# Revit family: MR-1002
name_source: partatom
category: Plumbing Fixtures
revit_build: Autodesk Revit 2014 (Build: 20130308_1515(x64)
units: mm (PartAtom-declared; Revit-internal decimal feet)

## types (1)
- MR-1002
    Brass Chromed = Brass
    CW Connection = Yes
    Data Sheet = http://helvex.com
    Description = Vértika Tub And/Or Shower Two Handle In-Wall Faucet
    Features = Threaded Body, Val-Vex Level Left And Right To ¼" Turn To Ceramic Disc; Includes Setting Tool For Maintenance
    HW Connection = Yes
    Inlet Threads = ½" - 14 NPT
    Installation Adjustment = 0.315" (8 mm) Max.
    Instructive = http://helvex.com
    Manufacturer = HELVEX
    Max. Working Pressure = 85.3 psi
    Min. Working Pressure = 2.9 psi
    Model = MR-1002
    Satin = Satín
    Total Height = 3"
    Total Length = 8"
    Total Width = 4"
    Type Comments = Shower Faucet
    URL = http://helvex.com

## geometry (parser evidence)
native form markers: Sweep x1
no freeform markers — native parametric forms only
